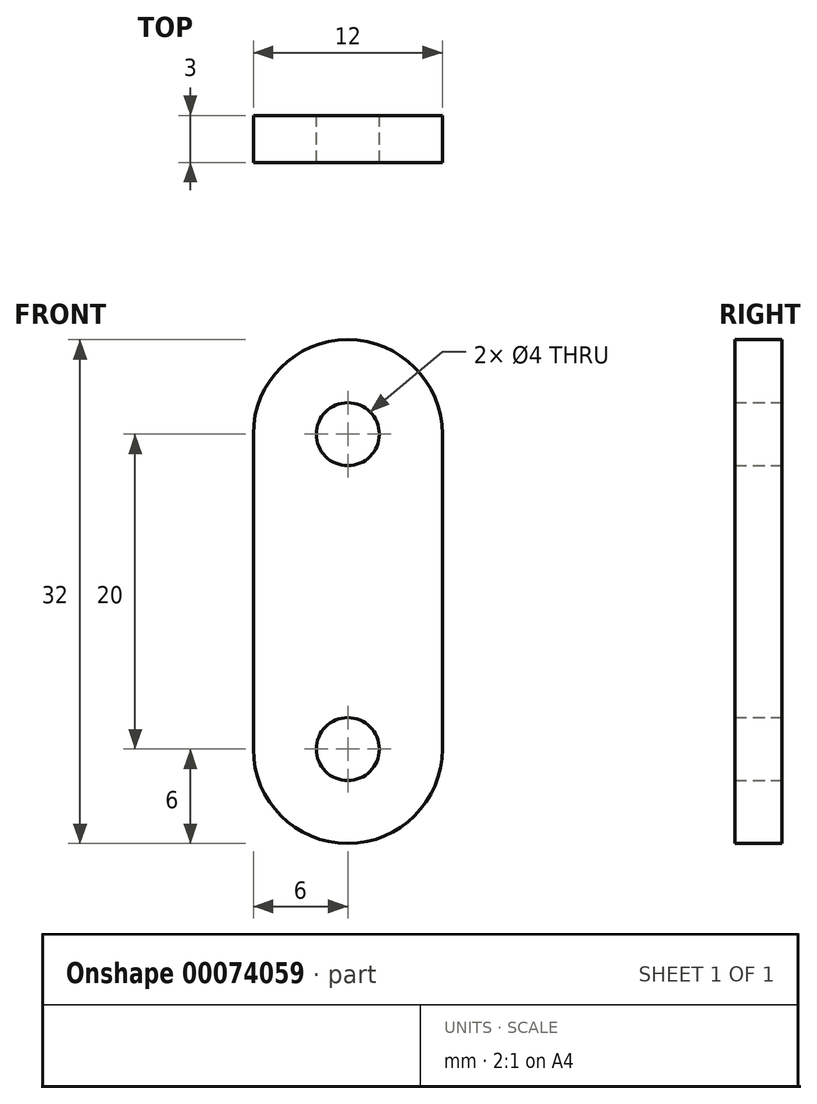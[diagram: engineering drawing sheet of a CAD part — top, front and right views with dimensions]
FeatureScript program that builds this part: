
annotation { "Feature Type Name" : "Feature", "Feature Type Description" : "" }
export const myFeature = defineFeature(function(context is Context, id is Id, definition is map)
    precondition{}
    {
        {
            var Q0;
            Q0=qCreatedBy(makeId("Front.planeOp"),FACE);
            var sketch = newSketch(context, id + "F0", { "sketchPlane" : qUnion([Q0])});
            skCircle(sketch, "E0", {"center": v(0, 0) * mm, "radius": 6 * mm});
            skCircle(sketch, "E1", {"center": v(0, -20) * mm, "radius": 6 * mm});
            skCircle(sketch, "E2", {"center": v(0, 0) * mm, "radius": 2 * mm});
            skCircle(sketch, "E3", {"center": v(0, -20) * mm, "radius": 2 * mm});
            skLineSegment(sketch, "E4", {"start": v(-6, 0) * mm, "end": v(-6, -20) * mm});
            skLineSegment(sketch, "E5", {"start": v(-6, -20) * mm, "end": v(6, -20) * mm});
            skLineSegment(sketch, "E6", {"start": v(6, -20) * mm, "end": v(6, 0) * mm});
            skLineSegment(sketch, "E7", {"start": v(6, 0) * mm, "end": v(-6, 0) * mm});
            skSolve(sketch);
        }
        {
            var Q0;
            Q0 = qSketchRegion(id + "F0", true);
            extrude(context, id + "F1", {"entities" : qUnion([Q0]), "depth" : 3 * mm});
        }
    });
